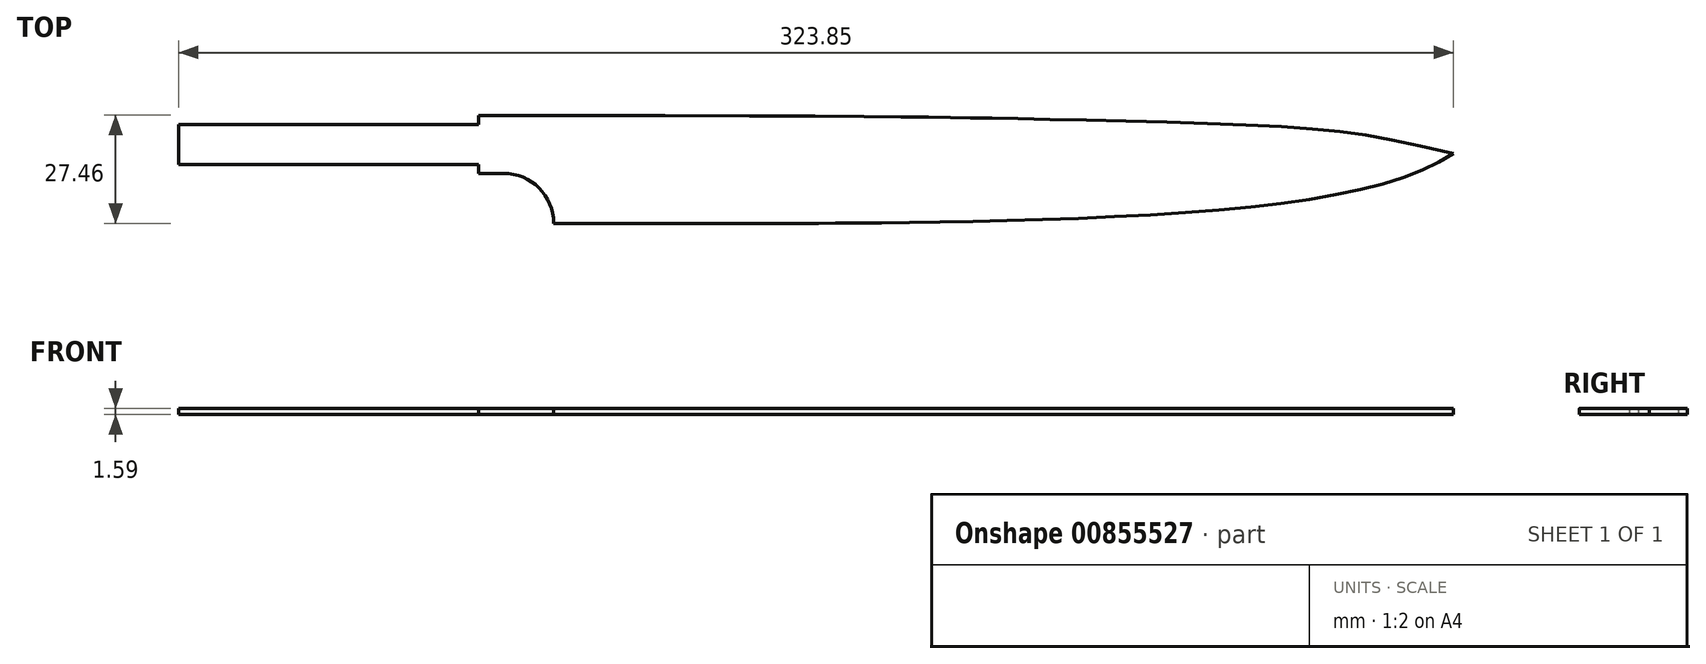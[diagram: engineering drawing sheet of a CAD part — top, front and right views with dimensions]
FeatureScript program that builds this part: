
annotation { "Feature Type Name" : "Feature", "Feature Type Description" : "" }
export const myFeature = defineFeature(function(context is Context, id is Id, definition is map)
    precondition{}
    {
        {
            var Q0;
            Q0=qCreatedBy(makeId("Top.planeOp"),FACE);
            var sketch = newSketch(context, id + "F0", { "sketchPlane" : qUnion([Q0])});
            skLineSegment(sketch, "E0.bottom", {"start": v(-47.47, -13.72) * mm, "end": v(-114.8, -13.72) * mm});
            skPoint(sketch, "E0.middle", {"position": v(0, 0) * mm});
            skFitSpline(sketch, "E1", {"points": [v(-113.81, 13.72) * mm, v(0, 12.9) * mm, v(70.98, 10.76) * mm, v(113.8, 4.03) * mm], "startDerivative": vector(702.58, -2.2) * mm, "endDerivative": vector(207.95, -49.8) * mm});
            skFitSpline(sketch, "E2", {"points": [v(-114.8, -13.72) * mm, v(-47.47, -13.72) * mm, v(53.18, -10.41) * mm, v(113.8, 4.03) * mm], "startDerivative": vector(594.5, -0.01) * mm, "endDerivative": vector(115.3, 78.27) * mm});
            skArc(sketch, "E3", {"start": v(-114.8, -13.72) * mm, "mid": v(-118.51, -4.74) * mm, "end": v(-127.5, -1.02) * mm});
            skLineSegment(sketch, "E4", {"start": v(-113.81, 13.72) * mm, "end": v(-133.84, 13.72) * mm});
            skLineSegment(sketch, "E5", {"start": v(-127.5, -1.02) * mm, "end": v(-133.84, -1.02) * mm});
            skLineSegment(sketch, "E6", {"start": v(-133.84, 13.72) * mm, "end": v(-133.84, 11.43) * mm});
            skPoint(sketch, "E7.orphan", {"position": v(-153.87, 13.72) * mm});
            skLineSegment(sketch, "E8.bottom", {"start": v(-133.84, 11.43) * mm, "end": v(-210.04, 11.43) * mm});
            skLineSegment(sketch, "E8.top", {"start": v(-133.84, 1.27) * mm, "end": v(-210.04, 1.27) * mm});
            skLineSegment(sketch, "E8.right", {"start": v(-210.04, 11.43) * mm, "end": v(-210.04, 1.27) * mm});
            skLineSegment(sketch, "E9.trimOffspring", {"start": v(-133.84, 1.27) * mm, "end": v(-133.84, -1.02) * mm});
            skSolve(sketch);
        }
        {
            var Q0;
            Q0 = qSketchRegion(id + "F0", true);
            extrude(context, id + "F1", {"entities" : qUnion([Q0]), "depth" : 1.59 * mm, "offsetDistance" : 25.4 * mm});
        }
    });
